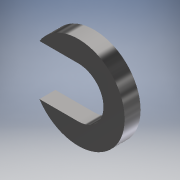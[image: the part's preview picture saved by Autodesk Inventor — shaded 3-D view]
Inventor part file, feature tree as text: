
AUTODESK INVENTOR PART (.ipt)
format: ipt  version: 2017 (Build 210142000, 142)  size: 104,448 bytes
history: native  units: in
note: dims shown in document units (in); Inventor stores cm internally (conversion verified against a paired STEP export)
features: extrude x1, sketch x1
ambient origin geometry x8: Origin, YZ Plane, XZ Plane, XY Plane, X Axis, Y Axis, Z Axis, Center Point
bodies: Solid1 (feature_tree)
feature tree (2):
  extrude  "Extrusion1"  Depth=0.3906in
  sketch  "Sketch1"  dims[d0=0.3594in d1=0.3906in d2=0.1235in d3=0.0in]
